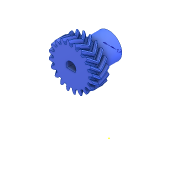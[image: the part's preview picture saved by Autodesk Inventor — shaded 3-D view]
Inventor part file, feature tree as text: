
AUTODESK INVENTOR PART (.ipt)
format: ipt  version: 2020.3 (Build 243373000, 373)  size: 1,519,104 bytes
history: native  units: mm
features: extrude x2, sketch x1, fillet x1, imported_body x1
ambient origin geometry x8: Origin, YZ Plane, XZ Plane, XY Plane, X Axis, Y Axis, Z Axis, Center Point
bodies: Solid1 (feature_tree)
feature tree (5):
  sketch  "Sketch1"  dims[d0=7.2mm d1=40.5mm d2=0.0mm d3=1.0mm d4=0.0mm d5=2.0mm]
  extrude  "Extrusion1"  Depth=2.0mm TaperAngle=0.0deg
  extrude  "Extrusion2"  Depth=1.0mm TaperAngle=0.0deg
  fillet  "Fillet1"  Radius=2.0mm
  imported_body  "Base1"
